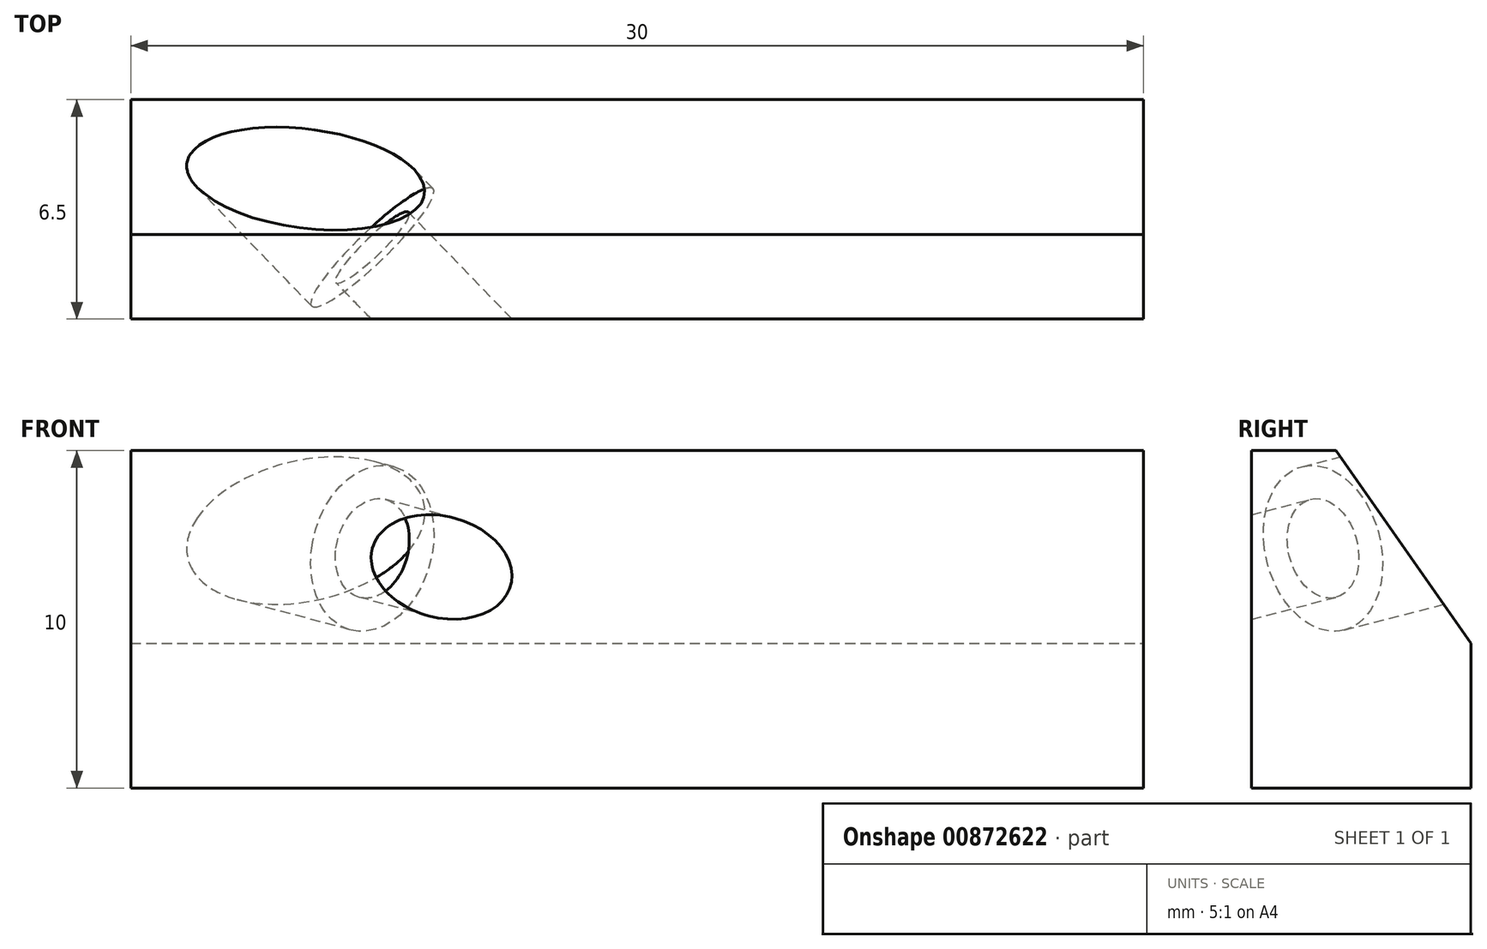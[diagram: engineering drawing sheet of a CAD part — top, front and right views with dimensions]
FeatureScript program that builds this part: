
annotation { "Feature Type Name" : "Feature", "Feature Type Description" : "" }
export const myFeature = defineFeature(function(context is Context, id is Id, definition is map)
    precondition{}
    {
        {
            var Q0;
            Q0=qCreatedBy(makeId("Front.planeOp"),FACE);
            var sketch = newSketch(context, id + "F0", { "sketchPlane" : qUnion([Q0])});
            skLineSegment(sketch, "E0.bottom", {"start": v(15, -5) * mm, "end": v(-15, -5) * mm});
            skLineSegment(sketch, "E0.top", {"start": v(15, 5) * mm, "end": v(-15, 5) * mm});
            skLineSegment(sketch, "E0.left", {"start": v(15, -5) * mm, "end": v(15, 5) * mm});
            skLineSegment(sketch, "E0.right", {"start": v(-15, -5) * mm, "end": v(-15, 5) * mm});
            skPoint(sketch, "E0.middle", {"position": v(0, 0) * mm});
            skSolve(sketch);
        }
        {
            var Q0;
            Q0=makeQuery(id+"F0.imprint","IMPRINT",FACE,{"disambiguationData":[TD([[makeQuery(id+"F0.imprint","IMPRINT",EDGE,{"derivedFrom":sQuery(id+"F0.wireOp",EDGE,"E0.bottom")}),-1.0]])]});
            extrude(context, id + "F1", {"entities" : qUnion([Q0]), "depth" : 6.5 * mm, "offsetDistance" : 25 * mm});
        }
        {
            var Q0;
            Q0=makeQuery(id+"F1.opExtrude","CAP_FACE",FACE,{"disambiguationData":[OSD([sQuery(id+"F0.wireOp",EDGE,"E0.bottom"),sQuery(id+"F0.wireOp",EDGE,"E0.top"),sQuery(id+"F0.wireOp",EDGE,"E0.left"),sQuery(id+"F0.wireOp",EDGE,"E0.right")])],"isStart":false});
            cPlane(context, id + "F2", {"entities" : qUnion([Q0]), "cplaneType" : CPlaneType.OFFSET, "offset" : 6 * mm, "width" : 150 * mm, "height" : 150 * mm});
        }
        {
            var Q0;
            Q0=qCreatedBy(id+"F2.planeOp",FACE);
            var sketch = newSketch(context, id + "F3", { "sketchPlane" : qUnion([Q0])});
            skLineSegment(sketch, "E1.bottom", {"start": v(4.19, -2.5) * mm, "end": v(-4.19, -2.5) * mm});
            skLineSegment(sketch, "E1.top", {"start": v(4.19, 2.5) * mm, "end": v(-4.19, 2.5) * mm});
            skLineSegment(sketch, "E1.left", {"start": v(4.19, -2.5) * mm, "end": v(4.19, 2.5) * mm});
            skLineSegment(sketch, "E1.right", {"start": v(-4.19, -2.5) * mm, "end": v(-4.19, 2.5) * mm});
            skPoint(sketch, "E1.middle", {"position": v(0, 0) * mm});
            skSolve(sketch);
        }
        {
            var Q0;
            Q0=qCreatedBy(makeId("Right.planeOp"),FACE);
            var sketch = newSketch(context, id + "F4", { "sketchPlane" : qUnion([Q0])});
            skLineSegment(sketch, "E2", {"start": v(0, 0) * mm, "end": v(-12.5, 0) * mm});
            skSolve(sketch);
        }
        {
            var Q0;
            Q0 = qBodyType(qCreatedBy(id + "F4" ,EDGE), BodyType.WIRE);
            cPlane(context, id + "F5", {"entities" : qUnion([Q0]), "cplaneType" : CPlaneType.LINE_ANGLE, "offset" : 25 * mm, "angle" : 15 * degree, "oppositeDirection" : true, "width" : 150 * mm, "height" : 150 * mm});
        }
        {
            var Q0;
            {var subQ0=sQuery(id+"F0.wireOp",EDGE,"E0.left");var subQ1=sQuery(id+"F0.wireOp",EDGE,"E0.top");Q0=makeQuery(id+"F13.boolean.opBoolean","SPLIT",EDGE,{"disambiguationData":[TD([makeQuery(id+"F1.opExtrude","SWEPT_FACE",FACE,{"disambiguationData":[OSD([subQ0])]})])],"derivedFrom":makeQuery(id+"F1.opExtrude","CAP_EDGE",EDGE,{"disambiguationData":[OSD([subQ1])],"isStart":true})});}
            chamfer(context, id + "F6", {"entities" : qUnion([Q0]), "chamferType" : ChamferType.OFFSET_ANGLE, "width" : 4 * mm, "oppositeDirection" : false, "angle" : 55 * degree, "tangentPropagation" : true});
        }
        {
            var Q0;
            Q0=qCreatedBy(id+"F5.planeOp",FACE);
            var sketch = newSketch(context, id + "F7", { "sketchPlane" : qUnion([Q0])});
            skLineSegment(sketch, "E3", {"start": v(0, 12.5) * mm, "end": v(-6, 6.5) * mm});
            skSolve(sketch);
        }
        {
            var Q0;
            Q0 = qBodyType(qCreatedBy(id + "F7" ,EDGE), BodyType.WIRE);
            var Q1;
            Q1=sQuery(id+"F7.wireOp",VERTEX,"E3.end");
            cPlane(context, id + "F8", {"entities" : qUnion([Q0, Q1]), "cplaneType" : CPlaneType.LINE_POINT, "offset" : 25 * mm, "width" : 150 * mm, "height" : 150 * mm});
        }
        {
            var Q0;
            Q0=qCreatedBy(id+"F8.planeOp",FACE);
            var sketch = newSketch(context, id + "F9", { "sketchPlane" : qUnion([Q0])});
            skCircle(sketch, "E4", {"center": v(8.27, 3.13) * mm, "radius": 1.5 * mm});
            skSolve(sketch);
        }
        {
            var Q0;
            Q0 = qSketchRegion(id + "F9", true);
            extrude(context, id + "F10", {"entities" : qUnion([Q0]), "operationType" : NewBodyOperationType.REMOVE, "endBound" : BoundingType.SYMMETRIC, "oppositeDirection" : true, "depth" : 25 * mm, "offsetDistance" : 25 * mm});
        }
        {
            var Q0;
            Q0=qCreatedBy(id+"F8.planeOp",FACE);
            cPlane(context, id + "F11", {"entities" : qUnion([Q0]), "cplaneType" : CPlaneType.OFFSET, "offset" : 25 * mm, "width" : 150 * mm, "height" : 150 * mm});
        }
        {
            var Q0;
            Q0=qCreatedBy(id+"F11.planeOp",FACE);
            var sketch = newSketch(context, id + "F12", { "sketchPlane" : qUnion([Q0])});
            skCircle(sketch, "E5", {"center": v(8.27, 3.13) * mm, "radius": 2.5 * mm});
            skSolve(sketch);
        }
        {
            var Q0;
            Q0 = qSketchRegion(id + "F12", true);
            extrude(context, id + "F13", {"entities" : qUnion([Q0]), "operationType" : NewBodyOperationType.REMOVE, "oppositeDirection" : true, "depth" : 22 * mm, "offsetDistance" : 25 * mm});
        }
    });
